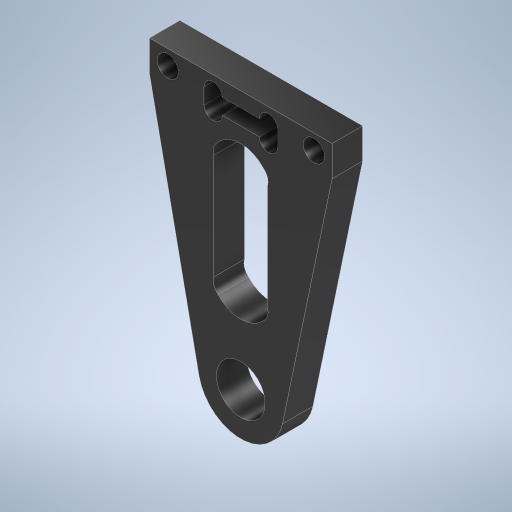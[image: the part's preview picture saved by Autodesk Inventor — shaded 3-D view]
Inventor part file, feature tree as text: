
AUTODESK INVENTOR PART (.ipt)
format: ipt  version: 2024.2 (Build 282272000, 272)  size: 311,296 bytes
history: native  units: mm
features: hole x2, sketch x1, extrude x1
ambient origin geometry x8: Origin, YZ Plane, XZ Plane, XY Plane, X Axis, Y Axis, Z Axis, Center Point
bodies: Solid1 (feature_tree)
feature tree (4):
  sketch  "Sketch1"  dims[d0=14.0mm d1=5.0mm d3=30.0mm d4=5.0mm d5=8.8mm d6=15.0mm d7=60.0deg d8=15.0mm d11=24.0mm d12=12.0mm d14=2.0mm d15=5.0mm d16=0.0mm d17=3.5mm d18=6.0mm d19=4.0mm d20=2.0mm d21=90.0deg d22=4.0mm d23=0.0mm d24=8.0mm d25=6.0mm d26=4.0mm d27=2.0mm d28=90.0deg d29=8.0mm d30=0.0mm d31=8.0mm d34=1.5mm d35=0.05mm d36=0.05mm d37=5.0mm d38=2.5mm d42=15.0mm d43=2.5mm]
  extrude  "Extrusion1"  Depth=5.0mm
  hole  "Hole1"  [1 undecoded]
  hole  "Hole2"  [1 undecoded]
note: 2 required parameter values undecoded (feature->parameter linkage not recoverable at this tier; creation-order binding heuristic only, values carry confidence <= 0.55)
